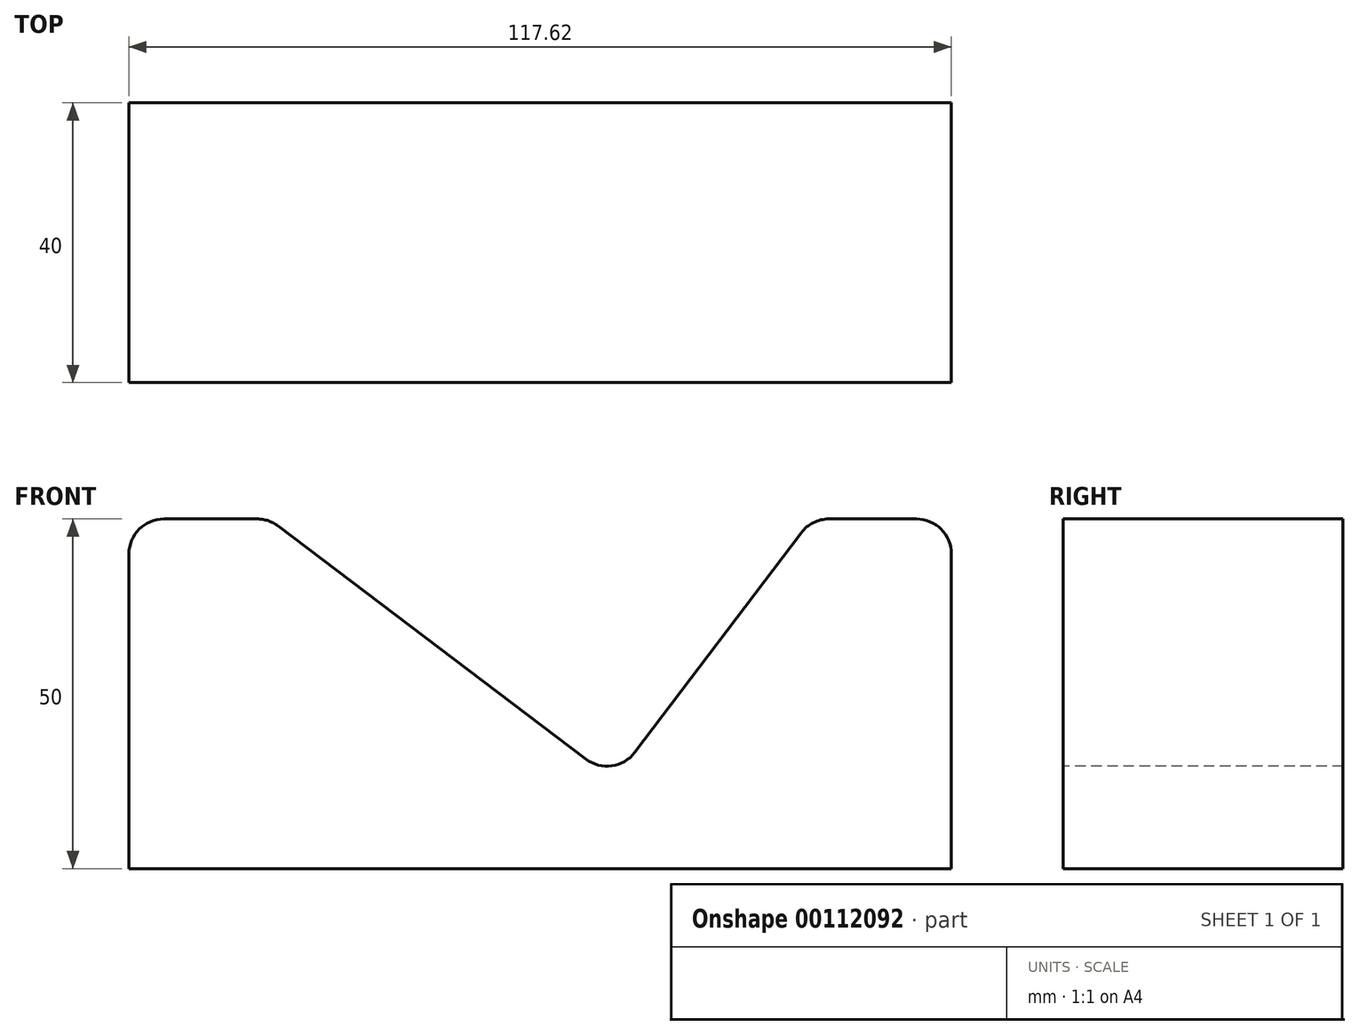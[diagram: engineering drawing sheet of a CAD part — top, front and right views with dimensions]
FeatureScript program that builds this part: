
annotation { "Feature Type Name" : "Feature", "Feature Type Description" : "" }
export const myFeature = defineFeature(function(context is Context, id is Id, definition is map)
    precondition{}
    {
        {
            var Q0;
            Q0=qCreatedBy(makeId("Front.planeOp"),FACE);
            var sketch = newSketch(context, id + "F0", { "sketchPlane" : qUnion([Q0])});
            skLineSegment(sketch, "E0.bottom", {"start": v(-69.33, 37.36) * mm, "end": v(48.29, 37.36) * mm});
            skLineSegment(sketch, "E0.top", {"start": v(-69.33, -12.64) * mm, "end": v(48.29, -12.64) * mm});
            skLineSegment(sketch, "E0.left", {"start": v(-69.33, 37.36) * mm, "end": v(-69.33, -12.64) * mm});
            skLineSegment(sketch, "E0.right", {"start": v(48.29, 37.36) * mm, "end": v(48.29, -12.64) * mm});
            skLineSegment(sketch, "E1", {"start": v(-49.33, 37.36) * mm, "end": v(0, 0) * mm});
            skLineSegment(sketch, "E2", {"start": v(0, 0) * mm, "end": v(28.29, 37.36) * mm});
            skSolve(sketch);
        }
        {
            var Q0;
            Q0=makeQuery(id+"F0.imprint","IMPRINT",FACE,{"disambiguationData":[TD([[makeQuery(id+"F0.imprint","IMPRINT",EDGE,{"derivedFrom":sQuery(id+"F0.wireOp",EDGE,"E0.top")}),1.0]])]});
            extrude(context, id + "F1", {"entities" : qUnion([Q0]), "depth" : 40 * mm});
        }
        {
            var Q0;
            Q0=makeQuery(id+"F1.opExtrude","SWEPT_EDGE",EDGE,{"disambiguationData":[OSD([sQuery(id+"F0.wireOp",EDGE,"E1"),sQuery(id+"F0.wireOp",EDGE,"E2")])]});
            fillet(context, id + "F2", {"entities" : qUnion([Q0]), "radius" : 5 * mm, "tangentPropagation" : true, "allowEdgeOverflow" : false});
        }
        {
            var Q0;
            Q0=makeQuery(id+"F1.opExtrude","SWEPT_EDGE",EDGE,{"disambiguationData":[OSD([sQuery(id+"F0.wireOp",EDGE,"E0.bottom"),sQuery(id+"F0.wireOp",EDGE,"E0.left")])]});
            var Q1;
            Q1=makeQuery(id+"F1.opExtrude","SWEPT_EDGE",EDGE,{"disambiguationData":[OSD([sQuery(id+"F0.wireOp",EDGE,"E0.bottom"),sQuery(id+"F0.wireOp",EDGE,"E0.right")])]});
            var Q2;
            Q2=makeQuery(id+"F1.opExtrude","SWEPT_EDGE",EDGE,{"disambiguationData":[OSD([sQuery(id+"F0.wireOp",EDGE,"E0.bottom"),sQuery(id+"F0.wireOp",EDGE,"E1")])]});
            var Q3;
            Q3=makeQuery(id+"F1.opExtrude","SWEPT_EDGE",EDGE,{"disambiguationData":[OSD([sQuery(id+"F0.wireOp",EDGE,"E0.bottom"),sQuery(id+"F0.wireOp",EDGE,"E2")])]});
            fillet(context, id + "F3", {"entities" : qUnion([Q0, Q1, Q2, Q3]), "radius" : 5 * mm, "tangentPropagation" : true, "allowEdgeOverflow" : false});
        }
    });
